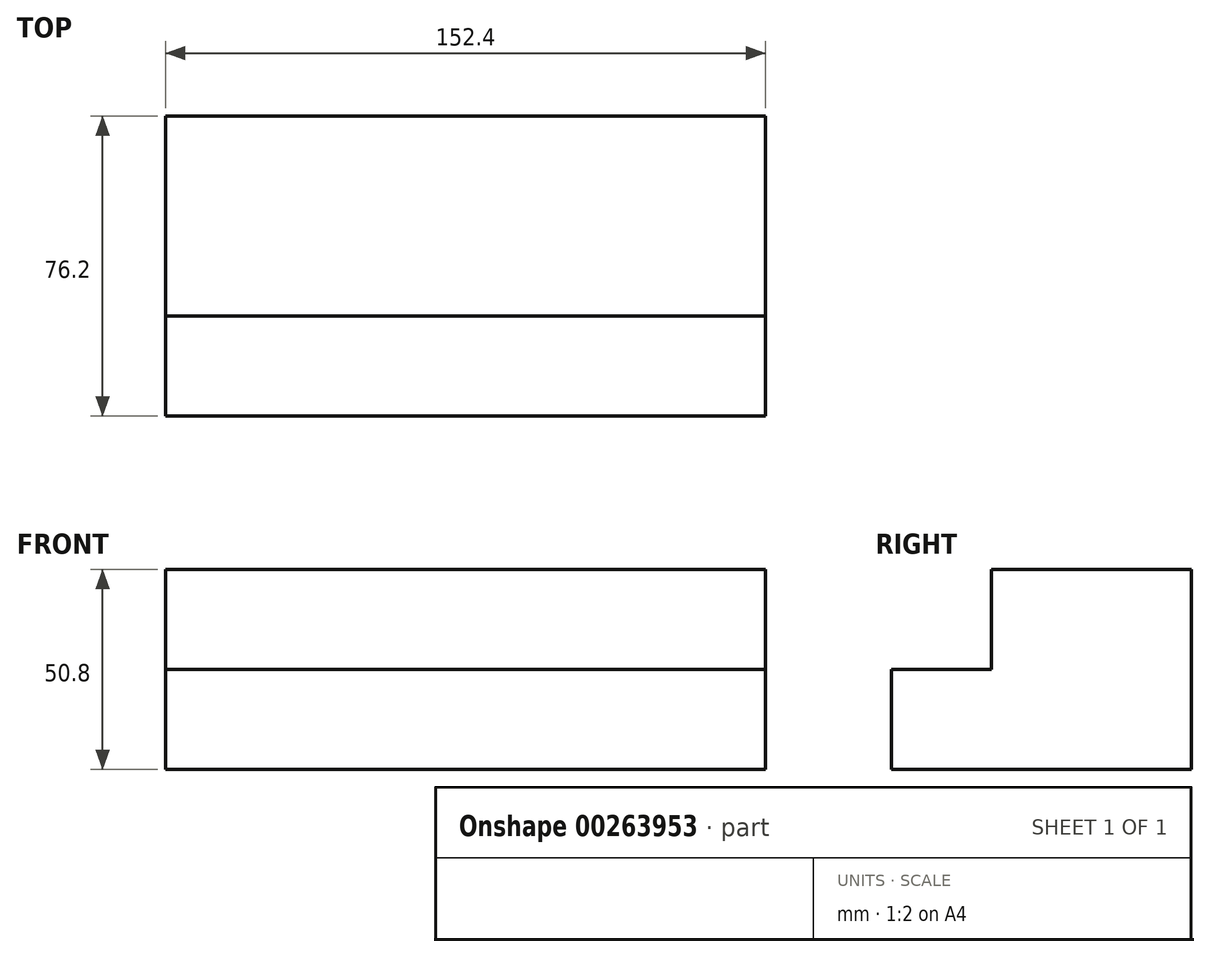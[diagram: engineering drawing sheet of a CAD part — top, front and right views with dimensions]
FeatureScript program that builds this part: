
annotation { "Feature Type Name" : "Feature", "Feature Type Description" : "" }
export const myFeature = defineFeature(function(context is Context, id is Id, definition is map)
    precondition{}
    {
        {
            var Q0;
            Q0=qCreatedBy(makeId("Right.planeOp"),FACE);
            var sketch = newSketch(context, id + "F0", { "sketchPlane" : qUnion([Q0])});
            skLineSegment(sketch, "E0.top", {"start": v(0, -50.8) * mm, "end": v(76.2, -50.8) * mm});
            skLineSegment(sketch, "E0.right", {"start": v(76.2, 0) * mm, "end": v(76.2, -50.8) * mm});
            skLineSegment(sketch, "E1", {"start": v(25.4, -25.4) * mm, "end": v(0, -25.4) * mm});
            skPoint(sketch, "E2.orphan", {"position": v(0, 0) * mm});
            skLineSegment(sketch, "E3", {"start": v(0, -25.4) * mm, "end": v(0, -50.8) * mm});
            skPoint(sketch, "E4.start.orphan", {"position": v(38.1, 0) * mm});
            skLineSegment(sketch, "E5", {"start": v(76.2, 0) * mm, "end": v(25.4, 0) * mm});
            skLineSegment(sketch, "E6", {"start": v(25.4, 0) * mm, "end": v(25.4, -25.4) * mm});
            skSolve(sketch);
        }
        {
            var Q0;
            Q0 = qSketchRegion(id + "F0", true);
            extrude(context, id + "F1", {"entities" : qUnion([Q0]), "depth" : 152.4 * mm});
        }
    });
